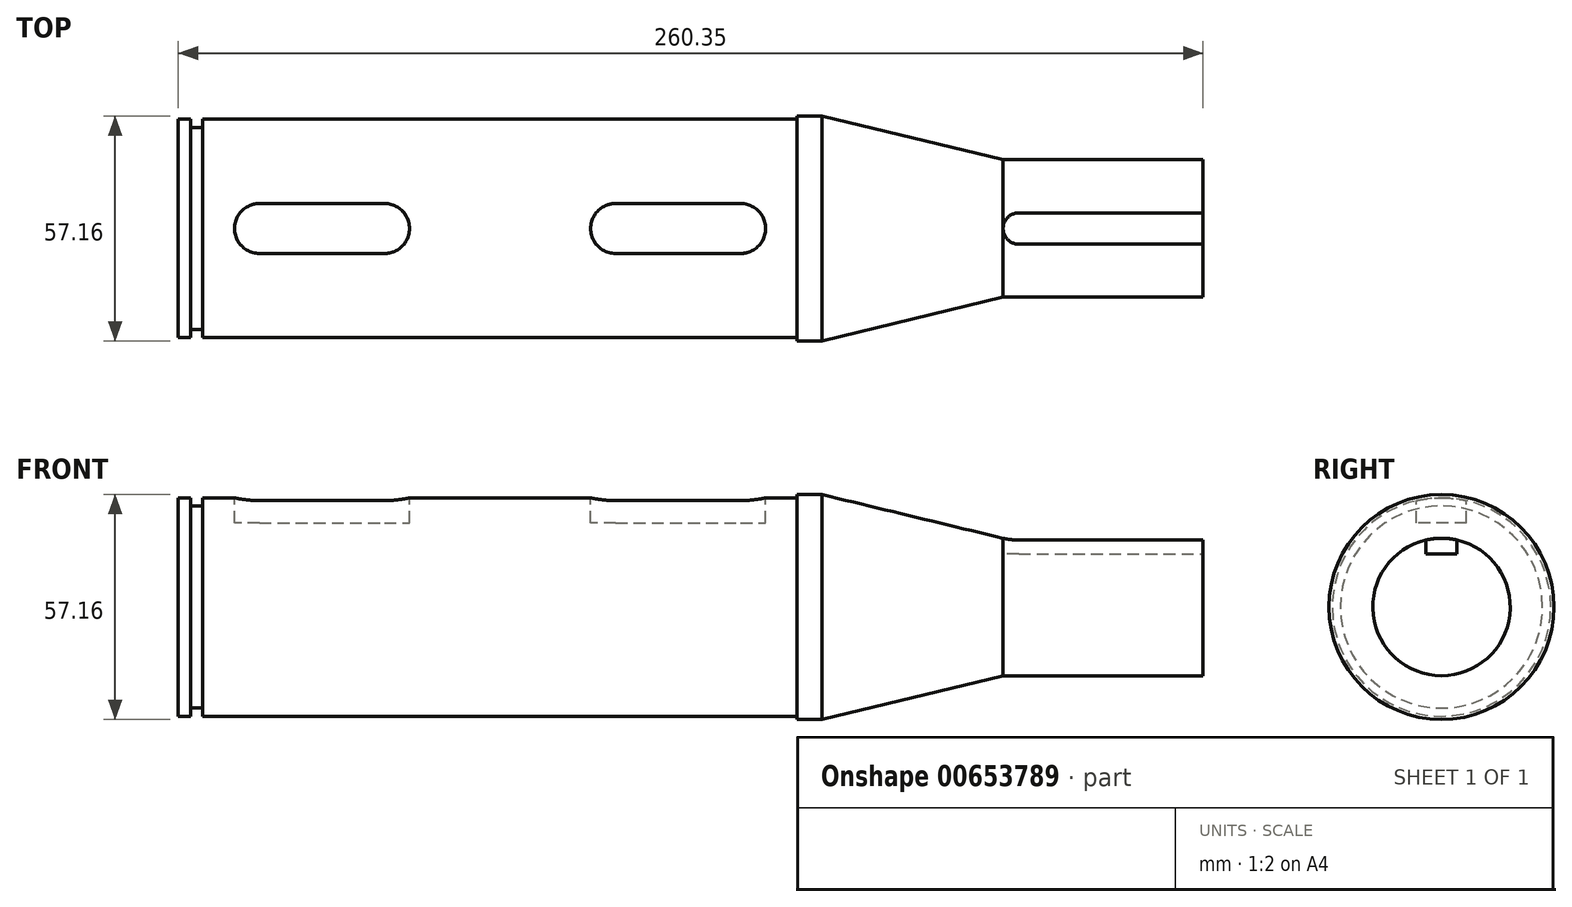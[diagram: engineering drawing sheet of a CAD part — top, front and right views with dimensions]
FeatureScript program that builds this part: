
annotation { "Feature Type Name" : "Feature", "Feature Type Description" : "" }
export const myFeature = defineFeature(function(context is Context, id is Id, definition is map)
    precondition{}
    {
        {
            var Q0;
            Q0=qCreatedBy(makeId("Front.planeOp"),FACE);
            var sketch = newSketch(context, id + "F0", { "sketchPlane" : qUnion([Q0])});
            skLineSegment(sketch, "E0", {"start": v(-157.18, 0) * mm, "end": v(-157.18, 27.75) * mm});
            skLineSegment(sketch, "E1", {"start": v(-157.18, 27.75) * mm, "end": v(-153.99, 27.75) * mm});
            skLineSegment(sketch, "E2", {"start": v(0, 27.75) * mm, "end": v(0, 28.58) * mm});
            skLineSegment(sketch, "E3", {"start": v(0, 28.58) * mm, "end": v(6.35, 28.58) * mm});
            skLineSegment(sketch, "E4", {"start": v(6.35, 28.58) * mm, "end": v(52.37, 17.46) * mm});
            skLineSegment(sketch, "E5", {"start": v(52.37, 17.46) * mm, "end": v(103.17, 17.46) * mm});
            skLineSegment(sketch, "E6", {"start": v(103.17, 17.46) * mm, "end": v(103.17, 0) * mm});
            skLineSegment(sketch, "E7", {"start": v(-153.99, 27.75) * mm, "end": v(-153.99, 25.68) * mm});
            skLineSegment(sketch, "E8", {"start": v(-153.99, 25.68) * mm, "end": v(-151, 25.68) * mm});
            skLineSegment(sketch, "E9", {"start": v(-151, 25.68) * mm, "end": v(-151, 27.75) * mm});
            skLineSegment(sketch, "E10.trimOffspring", {"start": v(-151, 27.75) * mm, "end": v(0, 27.75) * mm});
            skLineSegment(sketch, "E11", {"start": v(-157.18, 0) * mm, "end": v(103.17, 0) * mm});
            skSolve(sketch);
        }
        {
            var Q0;
            Q0 = qSketchRegion(id + "F0", true);
            var Q1;
            Q1=sQuery(id+"F0.wireOp",EDGE,"E11");
            revolve(context, id + "F1", {"entities" : qUnion([Q0]), "axis" : qUnion([Q1]), "revolveType" : RevolveType.FULL});
        }
        {
            var Q0;
            Q0=qCreatedBy(makeId("Top.planeOp"),FACE);
            cPlane(context, id + "F2", {"entities" : qUnion([Q0]), "cplaneType" : CPlaneType.OFFSET, "offset" : 27.75 * mm, "width" : 152.4 * mm, "height" : 152.4 * mm});
        }
        {
            var Q0;
            Q0=qCreatedBy(makeId("Top.planeOp"),FACE);
            cPlane(context, id + "F3", {"entities" : qUnion([Q0]), "cplaneType" : CPlaneType.OFFSET, "offset" : 17.46 * mm, "width" : 152.4 * mm, "height" : 152.4 * mm});
        }
        {
            var Q0;
            Q0=qCreatedBy(id+"F2.planeOp",FACE);
            var sketch = newSketch(context, id + "F4", { "sketchPlane" : qUnion([Q0])});
            skLineSegment(sketch, "E12.bottom", {"start": v(-136.54, 6.35) * mm, "end": v(-104.79, 6.35) * mm});
            skLineSegment(sketch, "E12.top", {"start": v(-136.54, -6.35) * mm, "end": v(-104.79, -6.35) * mm});
            skPoint(sketch, "E12.middle", {"position": v(-142.7, 0) * mm});
            skLineSegment(sketch, "E13.bottom", {"start": v(-46.05, 6.35) * mm, "end": v(-14.3, 6.35) * mm});
            skLineSegment(sketch, "E13.top", {"start": v(-46.05, -6.35) * mm, "end": v(-14.3, -6.35) * mm});
            skPoint(sketch, "E13.middle", {"position": v(-54.98, 0) * mm});
            skArc(sketch, "E14", {"start": v(-136.54, 6.35) * mm, "mid": v(-142.89, 0) * mm, "end": v(-136.54, -6.35) * mm});
            skArc(sketch, "E15", {"start": v(-104.79, -6.35) * mm, "mid": v(-98.44, 0) * mm, "end": v(-104.79, 6.35) * mm});
            skArc(sketch, "E16", {"start": v(-46.05, 6.35) * mm, "mid": v(-52.4, 0) * mm, "end": v(-46.05, -6.35) * mm});
            skArc(sketch, "E17", {"start": v(-14.3, -6.35) * mm, "mid": v(-7.95, 0) * mm, "end": v(-14.3, 6.35) * mm});
            skPoint(sketch, "E18.orphan", {"position": v(-126.92, 6.35) * mm});
            skPoint(sketch, "E19.orphan", {"position": v(-126.92, -6.35) * mm});
            skPoint(sketch, "E20.orphan", {"position": v(-158.47, 6.35) * mm});
            skPoint(sketch, "E21.orphan", {"position": v(-158.47, -6.35) * mm});
            skPoint(sketch, "E22.orphan", {"position": v(-72.33, 6.35) * mm});
            skPoint(sketch, "E23.orphan", {"position": v(-75.37, -6.35) * mm});
            skPoint(sketch, "E24.orphan", {"position": v(-34.58, 6.35) * mm});
            skPoint(sketch, "E25.orphan", {"position": v(-37.62, -6.35) * mm});
            skSolve(sketch);
        }
        {
            var Q0;
            Q0 = qSketchRegion(id + "F4", true);
            extrude(context, id + "F5", {"entities" : qUnion([Q0]), "operationType" : NewBodyOperationType.REMOVE, "oppositeDirection" : true, "depth" : 6.35 * mm, "offsetDistance" : 25.4 * mm});
        }
        {
            var Q0;
            Q0=qCreatedBy(id+"F3.planeOp",FACE);
            var sketch = newSketch(context, id + "F6", { "sketchPlane" : qUnion([Q0])});
            skLineSegment(sketch, "E26.bottom", {"start": v(56.34, 3.97) * mm, "end": v(103.17, 3.97) * mm});
            skLineSegment(sketch, "E26.top", {"start": v(56.34, -3.97) * mm, "end": v(103.17, -3.97) * mm});
            skLineSegment(sketch, "E26.right", {"start": v(103.17, 3.97) * mm, "end": v(103.17, -3.97) * mm});
            skPoint(sketch, "E26.middle", {"position": v(73.34, 0) * mm});
            skArc(sketch, "E27", {"start": v(56.34, 3.97) * mm, "mid": v(52.37, 0) * mm, "end": v(56.34, -3.97) * mm});
            skPoint(sketch, "E28.orphan", {"position": v(43.5, 3.97) * mm});
            skPoint(sketch, "E29.orphan", {"position": v(43.5, -3.97) * mm});
            skSolve(sketch);
        }
        {
            var Q0;
            Q0 = qSketchRegion(id + "F6", true);
            extrude(context, id + "F7", {"entities" : qUnion([Q0]), "operationType" : NewBodyOperationType.REMOVE, "oppositeDirection" : true, "depth" : 3.97 * mm, "offsetDistance" : 25.4 * mm});
        }
    });
